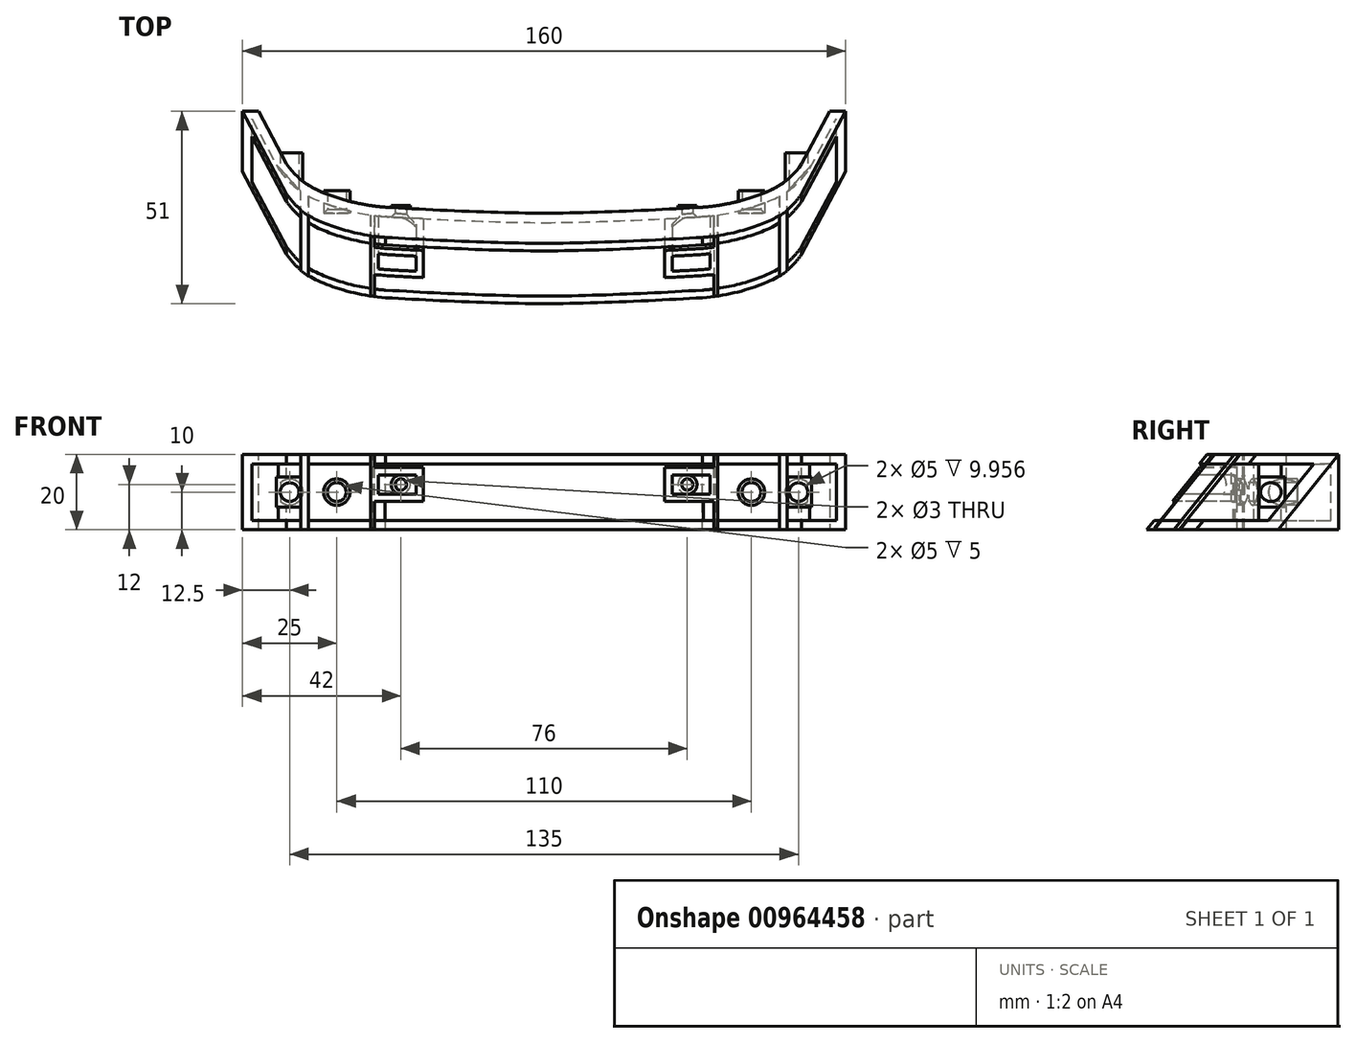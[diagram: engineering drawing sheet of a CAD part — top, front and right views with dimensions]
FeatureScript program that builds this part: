
annotation { "Feature Type Name" : "Feature", "Feature Type Description" : "" }
export const myFeature = defineFeature(function(context is Context, id is Id, definition is map)
    precondition{}
    {
        {
            var Q0;
            Q0=qCreatedBy(makeId("Top.planeOp"),FACE);
            var sketch = newSketch(context, id + "F0", { "sketchPlane" : qUnion([Q0])});
            skLineSegment(sketch, "E0", {"start": v(0, 34.5) * mm, "end": v(0, -43.78) * mm, "construction": true});
            skLineSegment(sketch, "E1", {"start": v(0, 0) * mm, "end": v(-102.6, 0) * mm, "construction": true});
            skLineSegment(sketch, "E2", {"start": v(-80, 0) * mm, "end": v(-80, 40.64) * mm, "construction": true});
            skLineSegment(sketch, "E3", {"start": v(-89.47, 35) * mm, "end": v(0, 35) * mm, "construction": true});
            skLineSegment(sketch, "E4", {"start": v(-80, 35) * mm, "end": v(-68.35, 13.09) * mm});
            skFitSpline(sketch, "E5", {"points": [v(-68.35, 13.09) * mm, v(-59.92, 6.04) * mm, v(-42.03, 1.57) * mm], "startDerivative": vector(19.42, -26.15) * mm, "endDerivative": vector(36.56, -2.64) * mm});
            skFitSpline(sketch, "E6", {"points": [v(-42.03, 1.57) * mm, v(0, 0) * mm], "startDerivative": vector(37.93, -2.25) * mm, "endDerivative": vector(36.74, 0) * mm});
            skPoint(sketch, "E7.orphan", {"position": v(-39.84, -10.44) * mm});
            skPoint(sketch, "E8.orphan", {"position": v(39.84, -10.44) * mm});
            skFitSpline(sketch, "E9.MirrorCS", {"points": [v(42.03, 1.57) * mm, v(0, 0) * mm], "startDerivative": vector(-37.93, -2.25) * mm, "endDerivative": vector(-36.74, 0) * mm});
            skFitSpline(sketch, "E10.MirrorCS", {"points": [v(68.35, 13.09) * mm, v(59.92, 6.04) * mm, v(42.03, 1.57) * mm], "startDerivative": vector(-19.42, -26.15) * mm, "endDerivative": vector(-36.56, -2.64) * mm});
            skLineSegment(sketch, "E11.MirrorCS", {"start": v(80, 35) * mm, "end": v(68.35, 13.09) * mm});
            skSolve(sketch);
        }
        {
            var Q0;
            Q0=qCreatedBy(makeId("Right.planeOp"),FACE);
            var sketch = newSketch(context, id + "F1", { "sketchPlane" : qUnion([Q0])});
            skLineSegment(sketch, "E12", {"start": v(50.4, 0) * mm, "end": v(8, 0) * mm, "construction": true});
            skLineSegment(sketch, "E13", {"start": v(-14.02, 5) * mm, "end": v(0, 5) * mm, "construction": true});
            skLineSegment(sketch, "E14", {"start": v(-14.02, -5) * mm, "end": v(0, -5) * mm, "construction": true});
            skLineSegment(sketch, "E15", {"start": v(0, 18.67) * mm, "end": v(0, 10) * mm, "construction": true});
            skLineSegment(sketch, "E16", {"start": v(8, 18.67) * mm, "end": v(8, -19.69) * mm, "construction": true});
            skLineSegment(sketch, "E17", {"start": v(50.4, -10) * mm, "end": v(-14.02, -10) * mm, "construction": true});
            skLineSegment(sketch, "E18", {"start": v(-14.02, 10) * mm, "end": v(0, 10) * mm, "construction": true});
            skLineSegment(sketch, "E19", {"start": v(0, -10) * mm, "end": v(16, 10) * mm});
            skLineSegment(sketch, "E20", {"start": v(0, -10) * mm, "end": v(24, -10) * mm});
            skLineSegment(sketch, "E21", {"start": v(24, -10) * mm, "end": v(24, 10) * mm});
            skLineSegment(sketch, "E22", {"start": v(24, 10) * mm, "end": v(16, 10) * mm});
            skLineSegment(sketch, "E23.trimOffspring", {"start": v(0, -10) * mm, "end": v(0, -19.69) * mm, "construction": true});
            skLineSegment(sketch, "E24.trimOffspring", {"start": v(4, -5) * mm, "end": v(50.4, -5) * mm, "construction": true});
            skLineSegment(sketch, "E25.trimOffspring", {"start": v(0, 0) * mm, "end": v(-14.02, 0) * mm, "construction": true});
            skLineSegment(sketch, "E26.trimOffspring", {"start": v(12, 5) * mm, "end": v(50.4, 5) * mm, "construction": true});
            skLineSegment(sketch, "E27.trimOffspring", {"start": v(16, 10) * mm, "end": v(50.4, 10) * mm, "construction": true});
            skLineSegment(sketch, "E28", {"start": v(0, -10) * mm, "end": v(0, 10) * mm});
            skLineSegment(sketch, "E29", {"start": v(16, 10) * mm, "end": v(0, 10) * mm});
            skLineSegment(sketch, "E30.bottom", {"start": v(0, 10) * mm, "end": v(-14.02, 10) * mm});
            skLineSegment(sketch, "E30.top", {"start": v(0, -10) * mm, "end": v(-14.02, -10) * mm});
            skLineSegment(sketch, "E30.left", {"start": v(0, 10) * mm, "end": v(0, -10) * mm});
            skLineSegment(sketch, "E30.right", {"start": v(-14.02, 10) * mm, "end": v(-14.02, -10) * mm});
            skSolve(sketch);
        }
        {
            var Q0;
            Q0=makeQuery(id+"F1.imprint","IMPRINT",FACE,{"disambiguationData":[TD([[makeQuery(id+"F1.imprint","IMPRINT",EDGE,{"derivedFrom":sQuery(id+"F1.wireOp",EDGE,"E19")}),-1.0]])]});
            var Q1;
            Q1=sQuery(id+"F0.wireOp",EDGE,"E4");
            var Q2;
            Q2=sQuery(id+"F0.wireOp",EDGE,"E5");
            var Q3;
            Q3=sQuery(id+"F0.wireOp",EDGE,"E6");
            var Q4;
            Q4=sQuery(id+"F0.wireOp",EDGE,"E9.MirrorCS");
            var Q5;
            Q5=sQuery(id+"F0.wireOp",EDGE,"E10.MirrorCS");
            var Q6;
            Q6=sQuery(id+"F0.wireOp",EDGE,"E11.MirrorCS");
            sweep(context, id + "F2", {"profiles" : qUnion([Q0]), "path" : qUnion([Q1, Q2, Q3, Q4, Q5, Q6]), "keepProfileOrientation" : true});
        }
        {
            var Q0;
            Q0=makeQuery(id+"F2.opSweep","SWEPT_FACE",FACE,{"disambiguationData":[OSD([sQuery(id+"F0.wireOp",EDGE,"E4"),sQuery(id+"F1.wireOp",EDGE,"E19")])]});
            var Q1;
            Q1=makeQuery(id+"F2.opSweep","SWEPT_FACE",FACE,{"disambiguationData":[OSD([sQuery(id+"F0.wireOp",EDGE,"E10.MirrorCS"),sQuery(id+"F1.wireOp",EDGE,"E19")])]});
            var Q2;
            Q2=makeQuery(id+"F2.opSweep","SWEPT_FACE",FACE,{"disambiguationData":[OSD([sQuery(id+"F0.wireOp",EDGE,"E11.MirrorCS"),sQuery(id+"F1.wireOp",EDGE,"E19")])]});
            var Q3;
            Q3=makeQuery(id+"F2.opSweep","SWEPT_FACE",FACE,{"disambiguationData":[OSD([sQuery(id+"F0.wireOp",EDGE,"E5"),sQuery(id+"F1.wireOp",EDGE,"E19")])]});
            var Q4;
            Q4=makeQuery(id+"F2.opSweep","SWEPT_FACE",FACE,{"disambiguationData":[OSD([sQuery(id+"F0.wireOp",EDGE,"E6"),sQuery(id+"F1.wireOp",EDGE,"E19")])]});
            var Q5;
            Q5=makeQuery(id+"F2.opSweep","SWEPT_FACE",FACE,{"disambiguationData":[OSD([sQuery(id+"F0.wireOp",EDGE,"E9.MirrorCS"),sQuery(id+"F1.wireOp",EDGE,"E19")])]});
            shell(context, id + "F3", {"entities" : qUnion([Q0, Q1, Q2, Q3, Q4, Q5]), "thickness" : 2.5 * mm});
        }
        {
            var Q0;
            Q0=qCreatedBy(makeId("Right.planeOp"),FACE);
            var sketch = newSketch(context, id + "F4", { "sketchPlane" : qUnion([Q0])});
            skLineSegment(sketch, "E31", {"start": v(0, 25.86) * mm, "end": v(0, -24.93) * mm, "construction": true});
            skLineSegment(sketch, "E32", {"start": v(51, 25.86) * mm, "end": v(51, -24.93) * mm, "construction": true});
            skLineSegment(sketch, "E33", {"start": v(59.89, 25.86) * mm, "end": v(59.89, -24.93) * mm, "construction": true});
            skLineSegment(sketch, "E34", {"start": v(59.89, -13.24) * mm, "end": v(59.89, 11.85) * mm, "construction": true});
            skLineSegment(sketch, "E35", {"start": v(51, 11.85) * mm, "end": v(51, -13.24) * mm, "construction": true});
            skLineSegment(sketch, "E36", {"start": v(59.89, 11.85) * mm, "end": v(59.89, -13.24) * mm});
            skLineSegment(sketch, "E37", {"start": v(51, -13.24) * mm, "end": v(51, 11.85) * mm});
            skLineSegment(sketch, "E38", {"start": v(59.89, 11.85) * mm, "end": v(51, 11.85) * mm});
            skLineSegment(sketch, "E39", {"start": v(51, -13.24) * mm, "end": v(59.89, -13.24) * mm});
            skSolve(sketch);
        }
        {
            var Q0;
            Q0=makeQuery(id+"F4.imprint","IMPRINT",FACE,{"disambiguationData":[TD([[makeQuery(id+"F4.imprint","IMPRINT",EDGE,{"derivedFrom":sQuery(id+"F4.wireOp",EDGE,"E36")}),-1.0]])]});
            extrude(context, id + "F5", {"entities" : qUnion([Q0]), "operationType" : NewBodyOperationType.REMOVE, "endBound" : BoundingType.SYMMETRIC, "oppositeDirection" : true, "depth" : 180 * mm, "offsetDistance" : 25 * mm});
        }
        {
            var Q0;
            Q0=qCreatedBy(makeId("Top.planeOp"),FACE);
            var sketch = newSketch(context, id + "F6", { "sketchPlane" : qUnion([Q0])});
            skLineSegment(sketch, "E40", {"start": v(0, 68.3) * mm, "end": v(0, -66) * mm, "construction": true});
            skLineSegment(sketch, "E41", {"start": v(-80, 68.3) * mm, "end": v(-80, -66) * mm, "construction": true});
            skLineSegment(sketch, "E42", {"start": v(80, 68.3) * mm, "end": v(80, -66) * mm, "construction": true});
            skLineSegment(sketch, "E43", {"start": v(-45, 25.93) * mm, "end": v(-46, 25.93) * mm});
            skLineSegment(sketch, "E44", {"start": v(-46, 25.93) * mm, "end": v(-46, 2.04) * mm});
            skLineSegment(sketch, "E45", {"start": v(-46, 2.04) * mm, "end": v(-45, 2.04) * mm});
            skLineSegment(sketch, "E46", {"start": v(-45, 2.04) * mm, "end": v(-45, 25.93) * mm});
            skLineSegment(sketch, "E47.MirrorCS", {"start": v(45, 25.93) * mm, "end": v(46, 25.93) * mm});
            skLineSegment(sketch, "E48.MirrorCS", {"start": v(46, 25.93) * mm, "end": v(46, 2.04) * mm, "construction": true});
            skLineSegment(sketch, "E49.MirrorCS", {"start": v(45, 25.93) * mm, "end": v(45, 2.04) * mm, "construction": true});
            skLineSegment(sketch, "E50", {"start": v(-45, 25.93) * mm, "end": v(-45, 2.04) * mm});
            skLineSegment(sketch, "E51.MirrorCS", {"start": v(46, 2.04) * mm, "end": v(45, 2.04) * mm});
            skPoint(sketch, "E52.orphan", {"position": v(-45, 68.3) * mm});
            skPoint(sketch, "E53.orphan", {"position": v(-46, 68.3) * mm});
            skPoint(sketch, "E54.orphan", {"position": v(-46, -66) * mm});
            skPoint(sketch, "E55.orphan", {"position": v(-45, -66) * mm});
            skLineSegment(sketch, "E56.MirrorCS", {"start": v(45, 25.93) * mm, "end": v(45, 2.04) * mm});
            skLineSegment(sketch, "E57.MirrorCS", {"start": v(46, 25.93) * mm, "end": v(46, 2.04) * mm});
            skPoint(sketch, "E58.orphan", {"position": v(46, 68.3) * mm});
            skPoint(sketch, "E59.orphan", {"position": v(45, 68.3) * mm});
            skPoint(sketch, "E60.orphan", {"position": v(45, -66) * mm});
            skPoint(sketch, "E61.orphan", {"position": v(46, -66) * mm});
            skSolve(sketch);
        }
        {
            var Q0;
            Q0 = qSketchRegion(id + "F6", true);
            extrude(context, id + "F7", {"entities" : qUnion([Q0]), "operationType" : NewBodyOperationType.ADD, "endBound" : BoundingType.SYMMETRIC, "depth" : 20 * mm, "offsetDistance" : 25 * mm});
        }
        {
            var Q0;
            Q0=makeQuery(id+"F7.opExtrude","SWEPT_FACE",FACE,{"disambiguationData":[OSD([sQuery(id+"F6.wireOp",EDGE,"E44")])]});
            var sketch = newSketch(context, id + "F8", { "sketchPlane" : qUnion([Q0])});
            skLineSegment(sketch, "E62", {"start": v(-18, 10) * mm, "end": v(-2.04, 10) * mm});
            skLineSegment(sketch, "E63", {"start": v(-2.04, 10) * mm, "end": v(-2.04, -9.96) * mm});
            skLineSegment(sketch, "E64", {"start": v(-2.04, -9.96) * mm, "end": v(-18, 10) * mm});
            skSolve(sketch);
        }
        {
            var Q0;
            Q0=qCreatedBy(makeId("Front.planeOp"),FACE);
            var sketch = newSketch(context, id + "F9", { "sketchPlane" : qUnion([Q0])});
            skLineSegment(sketch, "E65", {"start": v(0, 13.76) * mm, "end": v(0, -16.88) * mm, "construction": true});
            skLineSegment(sketch, "E66", {"start": v(-46, 6.5) * mm, "end": v(-46, -2.5) * mm});
            skLineSegment(sketch, "E67", {"start": v(-46, -2.5) * mm, "end": v(-32, -2.5) * mm});
            skLineSegment(sketch, "E68", {"start": v(-32, -2.5) * mm, "end": v(-32, 6.5) * mm});
            skLineSegment(sketch, "E69", {"start": v(-32, 6.5) * mm, "end": v(-46, 6.5) * mm});
            skLineSegment(sketch, "E70", {"start": v(-44, 4.5) * mm, "end": v(-44, -0.5) * mm});
            skLineSegment(sketch, "E71", {"start": v(-44, -0.5) * mm, "end": v(-34, -0.5) * mm});
            skLineSegment(sketch, "E72", {"start": v(-34, -0.5) * mm, "end": v(-34, 4.5) * mm});
            skLineSegment(sketch, "E73", {"start": v(-34, 4.5) * mm, "end": v(-44, 4.5) * mm});
            skLineSegment(sketch, "E74.MirrorCS", {"start": v(32, 6.5) * mm, "end": v(46, 6.5) * mm});
            skLineSegment(sketch, "E75.MirrorCS", {"start": v(46, 6.5) * mm, "end": v(46, -2.5) * mm});
            skLineSegment(sketch, "E76.MirrorCS", {"start": v(46, -2.5) * mm, "end": v(32, -2.5) * mm});
            skLineSegment(sketch, "E77.MirrorCS", {"start": v(32, -2.5) * mm, "end": v(32, 6.5) * mm});
            skLineSegment(sketch, "E78.MirrorCS", {"start": v(34, -0.5) * mm, "end": v(34, 4.5) * mm});
            skLineSegment(sketch, "E79.MirrorCS", {"start": v(34, 4.5) * mm, "end": v(44, 4.5) * mm});
            skLineSegment(sketch, "E80.MirrorCS", {"start": v(44, 4.5) * mm, "end": v(44, -0.5) * mm});
            skLineSegment(sketch, "E81.MirrorCS", {"start": v(44, -0.5) * mm, "end": v(34, -0.5) * mm});
            skLineSegment(sketch, "E82", {"start": v(-81.56, 0) * mm, "end": v(83.03, 0) * mm, "construction": true});
            skSolve(sketch);
        }
        {
            var Q0;
            Q0 = qSketchRegion(id + "F9", true);
            var Q1;
            Q1=makeQuery(id+"F9.imprint","IMPRINT",FACE,{"disambiguationData":[TD([[makeQuery(id+"F9.imprint","IMPRINT",EDGE,{"derivedFrom":sQuery(id+"F9.wireOp",EDGE,"E66")}),1.0]])]});
            extrude(context, id + "F10", {"entities" : qUnion([Q0, Q1]), "operationType" : NewBodyOperationType.ADD, "oppositeDirection" : true, "depth" : 24.5 * mm, "offsetDistance" : 25 * mm});
        }
        {
            var Q0;
            Q0=qCreatedBy(makeId("Right.planeOp"),FACE);
            var sketch = newSketch(context, id + "F11", { "sketchPlane" : qUnion([Q0])});
            skLineSegment(sketch, "E83.bottom", {"start": v(-5.65, 10.74) * mm, "end": v(2.01, 10.74) * mm});
            skLineSegment(sketch, "E83.top", {"start": v(-5.65, -6.02) * mm, "end": v(2.01, -6.02) * mm});
            skLineSegment(sketch, "E83.left", {"start": v(-5.65, 10.74) * mm, "end": v(-5.65, -6.02) * mm});
            skLineSegment(sketch, "E83.right", {"start": v(2.01, 10.74) * mm, "end": v(2.01, -6.02) * mm});
            skSolve(sketch);
        }
        {
            var Q0;
            Q0 = qSketchRegion(id + "F11", true);
            extrude(context, id + "F12", {"entities" : qUnion([Q0]), "operationType" : NewBodyOperationType.REMOVE, "endBound" : BoundingType.SYMMETRIC, "depth" : 100 * mm, "offsetDistance" : 25 * mm});
        }
        {
            var Q0;
            Q0=qCreatedBy(makeId("Front.planeOp"),FACE);
            var sketch = newSketch(context, id + "F13", { "sketchPlane" : qUnion([Q0])});
            skLineSegment(sketch, "E84", {"start": v(0, 29.7) * mm, "end": v(0, -29.07) * mm, "construction": true});
            skLineSegment(sketch, "E85", {"start": v(62.5, 29.7) * mm, "end": v(62.5, -29.07) * mm, "construction": true});
            skLineSegment(sketch, "E86", {"start": v(-83.37, 0) * mm, "end": v(0, 0) * mm, "construction": true});
            skLineSegment(sketch, "E87", {"start": v(-62.5, 10) * mm, "end": v(-64.5, 10) * mm});
            skLineSegment(sketch, "E88", {"start": v(-64.5, 10) * mm, "end": v(-64.5, -10) * mm});
            skLineSegment(sketch, "E89", {"start": v(-64.5, -10) * mm, "end": v(-62.5, -10) * mm});
            skLineSegment(sketch, "E90", {"start": v(-62.5, -10) * mm, "end": v(-62.5, 10) * mm});
            skLineSegment(sketch, "E91.MirrorCS", {"start": v(62.5, -10) * mm, "end": v(62.5, 10) * mm});
            skLineSegment(sketch, "E92.MirrorCS", {"start": v(62.5, 10) * mm, "end": v(64.5, 10) * mm});
            skLineSegment(sketch, "E93.MirrorCS", {"start": v(64.5, 10) * mm, "end": v(64.5, -10) * mm});
            skLineSegment(sketch, "E94.MirrorCS", {"start": v(64.5, -10) * mm, "end": v(62.5, -10) * mm});
            skSolve(sketch);
        }
        {
            var Q0;
            Q0 = qSketchRegion(id + "F13", true);
            extrude(context, id + "F14", {"entities" : qUnion([Q0]), "operationType" : NewBodyOperationType.ADD, "oppositeDirection" : true, "depth" : 30 * mm, "offsetDistance" : 25 * mm});
        }
        {
            var Q0;
            Q0=qCreatedBy(makeId("Top.planeOp"),FACE);
            var sketch = newSketch(context, id + "F15", { "sketchPlane" : qUnion([Q0])});
            skFitSpline(sketch, "E95", {"points": [v(-29.25, 0.78) * mm, v(-42.32, 1.47) * mm, v(-47.66, 2.15) * mm, v(-54.7, 3.85) * mm, v(-61.26, 6.5) * mm, v(-65.24, 9.27) * mm], "startDerivative": vector(-54.73, 2.37) * mm, "endDerivative": vector(-22.49, 17.56) * mm});
            skFitSpline(sketch, "E96", {"points": [v(-29.25, 0.78) * mm, v(-21.3, 0.42) * mm, v(0, 0) * mm], "startDerivative": vector(18.42, -1.02) * mm, "endDerivative": vector(39.34, 0) * mm});
            skLineSegment(sketch, "E97", {"start": v(0, 31.46) * mm, "end": v(0, -16.2) * mm, "construction": true});
            skFitSpline(sketch, "E98.MirrorCS", {"points": [v(29.25, 0.78) * mm, v(21.3, 0.42) * mm, v(0, 0) * mm], "startDerivative": vector(-18.42, -1.02) * mm, "endDerivative": vector(-39.34, 0) * mm});
            skFitSpline(sketch, "E99.MirrorCS", {"points": [v(29.25, 0.78) * mm, v(42.32, 1.47) * mm, v(47.66, 2.15) * mm, v(54.7, 3.85) * mm, v(61.26, 6.5) * mm, v(65.24, 9.27) * mm], "startDerivative": vector(54.73, 2.37) * mm, "endDerivative": vector(22.49, 17.56) * mm});
            skSolve(sketch);
        }
        {
            var Q0;
            Q0=makeQuery(id+"F1.imprint","IMPRINT",FACE,{"disambiguationData":[TD([[makeQuery(id+"F1.imprint","IMPRINT",EDGE,{"derivedFrom":sQuery(id+"F1.wireOp",EDGE,"E19")}),1.0]])]});
            var Q1;
            Q1=makeQuery(id+"F1.imprint","IMPRINT",FACE,{"disambiguationData":[TD([[makeQuery(id+"F1.imprint","IMPRINT",EDGE,{"derivedFrom":sQuery(id+"F1.wireOp",EDGE,"E30.bottom")}),1.0]])]});
            var Q2;
            Q2 = qConstructionFilter(qBodyType(qCreatedBy(id + "F15" ,EDGE), BodyType.WIRE), ConstructionObject.NO);
            sweep(context, id + "F16", {"operationType" : NewBodyOperationType.REMOVE, "profiles" : qUnion([Q0, Q1]), "path" : qUnion([Q2]), "keepProfileOrientation" : true});
        }
        {
            var Q0;
            Q0=qCreatedBy(makeId("Front.planeOp"),FACE);
            var sketch = newSketch(context, id + "F17", { "sketchPlane" : qUnion([Q0])});
            skLineSegment(sketch, "E100", {"start": v(-87.14, 0) * mm, "end": v(85.86, 0) * mm, "construction": true});
            skLineSegment(sketch, "E101", {"start": v(-51.82, 2) * mm, "end": v(50.18, 2) * mm, "construction": true});
            skLineSegment(sketch, "E102", {"start": v(-55, 21.02) * mm, "end": v(-55, -28.71) * mm, "construction": true});
            skLineSegment(sketch, "E103", {"start": v(55, 20.84) * mm, "end": v(55, -28.17) * mm, "construction": true});
            skLineSegment(sketch, "E104", {"start": v(-67.5, 21.56) * mm, "end": v(-67.5, -28.17) * mm, "construction": true});
            skLineSegment(sketch, "E105", {"start": v(67.5, 22.28) * mm, "end": v(67.5, -28.53) * mm, "construction": true});
            skLineSegment(sketch, "E106", {"start": v(-38, 22.1) * mm, "end": v(-38, -28.17) * mm, "construction": true});
            skLineSegment(sketch, "E107", {"start": v(38, 22.1) * mm, "end": v(38, -27.63) * mm, "construction": true});
            skCircle(sketch, "E108", {"center": v(-55, 0) * mm, "radius": 2.5 * mm});
            skCircle(sketch, "E109", {"center": v(-67.5, 0) * mm, "radius": 2.5 * mm});
            skCircle(sketch, "E110", {"center": v(-38, 2) * mm, "radius": 1.5 * mm});
            skCircle(sketch, "E111", {"center": v(38, 2) * mm, "radius": 1.5 * mm});
            skCircle(sketch, "E112", {"center": v(55, 0) * mm, "radius": 2.5 * mm});
            skCircle(sketch, "E113", {"center": v(67.5, 0) * mm, "radius": 2.5 * mm});
            skLineSegment(sketch, "E114", {"start": v(0, 20.99) * mm, "end": v(0, -27.5) * mm, "construction": true});
            skCircle(sketch, "E115", {"center": v(-67.5, 0) * mm, "radius": 3.5 * mm});
            skCircle(sketch, "E116", {"center": v(-55, 0) * mm, "radius": 3.5 * mm});
            skCircle(sketch, "E117", {"center": v(-38, 2) * mm, "radius": 2.5 * mm});
            skCircle(sketch, "E118.MirrorC", {"center": v(38, 2) * mm, "radius": 2.5 * mm});
            skCircle(sketch, "E119.MirrorC", {"center": v(55, 0) * mm, "radius": 3.5 * mm});
            skCircle(sketch, "E120.MirrorC", {"center": v(67.5, 0) * mm, "radius": 3.5 * mm});
            skSolve(sketch);
        }
        {
            var Q0;
            Q0=makeQuery(id+"F17.imprint","IMPRINT",FACE,{"disambiguationData":[TD([[makeQuery(id+"F17.imprint","IMPRINT",EDGE,{"derivedFrom":sQuery(id+"F17.wireOp",EDGE,"E108")}),1.0]])]});
            var Q1;
            Q1=makeQuery(id+"F17.imprint","IMPRINT",FACE,{"disambiguationData":[TD([[makeQuery(id+"F17.imprint","IMPRINT",EDGE,{"derivedFrom":sQuery(id+"F17.wireOp",EDGE,"E109")}),1.0]])]});
            var Q2;
            Q2=makeQuery(id+"F17.imprint","IMPRINT",FACE,{"disambiguationData":[TD([[makeQuery(id+"F17.imprint","IMPRINT",EDGE,{"derivedFrom":sQuery(id+"F17.wireOp",EDGE,"E110")}),1.0]])]});
            var Q3;
            Q3=makeQuery(id+"F17.imprint","IMPRINT",FACE,{"disambiguationData":[TD([[makeQuery(id+"F17.imprint","IMPRINT",EDGE,{"derivedFrom":sQuery(id+"F17.wireOp",EDGE,"E111")}),1.0]])]});
            var Q4;
            Q4=makeQuery(id+"F17.imprint","IMPRINT",FACE,{"disambiguationData":[TD([[makeQuery(id+"F17.imprint","IMPRINT",EDGE,{"derivedFrom":sQuery(id+"F17.wireOp",EDGE,"E112")}),1.0]])]});
            var Q5;
            Q5=makeQuery(id+"F17.imprint","IMPRINT",FACE,{"disambiguationData":[TD([[makeQuery(id+"F17.imprint","IMPRINT",EDGE,{"derivedFrom":sQuery(id+"F17.wireOp",EDGE,"E113")}),1.0]])]});
            extrude(context, id + "F18", {"entities" : qUnion([Q0, Q1, Q2, Q3, Q4, Q5]), "operationType" : NewBodyOperationType.REMOVE, "oppositeDirection" : true, "depth" : 45 * mm, "offsetDistance" : 25 * mm});
        }
        {
            var Q0;
            Q0=qCreatedBy(makeId("Front.planeOp"),FACE);
            var sketch = newSketch(context, id + "F19", { "sketchPlane" : qUnion([Q0])});
            skLineSegment(sketch, "E121", {"start": v(-85.37, 0) * mm, "end": v(87.63, 0) * mm, "construction": true});
            skLineSegment(sketch, "E122", {"start": v(-50.04, 2) * mm, "end": v(51.95, 2) * mm, "construction": true});
            skLineSegment(sketch, "E123", {"start": v(-55, 21.02) * mm, "end": v(-55, -28.71) * mm, "construction": true});
            skLineSegment(sketch, "E124", {"start": v(55, 20.84) * mm, "end": v(55, -28.17) * mm, "construction": true});
            skLineSegment(sketch, "E125", {"start": v(-67.5, 21.56) * mm, "end": v(-67.5, -28.17) * mm, "construction": true});
            skLineSegment(sketch, "E126", {"start": v(67.5, 22.28) * mm, "end": v(67.5, -28.53) * mm, "construction": true});
            skLineSegment(sketch, "E127", {"start": v(-38, 22.1) * mm, "end": v(-38, -28.17) * mm, "construction": true});
            skLineSegment(sketch, "E128", {"start": v(38, 22.1) * mm, "end": v(38, -27.63) * mm, "construction": true});
            skCircle(sketch, "E129", {"center": v(-38, 2) * mm, "radius": 1.5 * mm});
            skCircle(sketch, "E130", {"center": v(38, 2) * mm, "radius": 1.5 * mm});
            skLineSegment(sketch, "E131", {"start": v(0, 20.99) * mm, "end": v(0, -27.5) * mm, "construction": true});
            skCircle(sketch, "E132", {"center": v(-38, 2) * mm, "radius": 2.5 * mm});
            skCircle(sketch, "E133.MirrorC", {"center": v(38, 2) * mm, "radius": 2.5 * mm});
            skSolve(sketch);
        }
        {
            var Q0;
            Q0=qCreatedBy(makeId("Front.planeOp"),FACE);
            var sketch = newSketch(context, id + "F20", { "sketchPlane" : qUnion([Q0])});
            skLineSegment(sketch, "E134", {"start": v(-87.14, 0) * mm, "end": v(85.86, 0) * mm, "construction": true});
            skLineSegment(sketch, "E135", {"start": v(-51.82, 2) * mm, "end": v(50.18, 2) * mm, "construction": true});
            skLineSegment(sketch, "E136", {"start": v(-55, -4.97) * mm, "end": v(-55, -54.71) * mm, "construction": true});
            skLineSegment(sketch, "E137", {"start": v(55, -5.15) * mm, "end": v(55, -54.17) * mm, "construction": true});
            skLineSegment(sketch, "E138", {"start": v(-67.5, -4.43) * mm, "end": v(-67.5, -54.17) * mm, "construction": true});
            skLineSegment(sketch, "E139", {"start": v(67.5, -3.71) * mm, "end": v(67.5, -54.53) * mm, "construction": true});
            skLineSegment(sketch, "E140", {"start": v(-38, -3.9) * mm, "end": v(-38, -54.17) * mm, "construction": true});
            skLineSegment(sketch, "E141", {"start": v(38, -3.9) * mm, "end": v(38, -53.63) * mm, "construction": true});
            skCircle(sketch, "E142", {"center": v(-55, 0) * mm, "radius": 2.5 * mm});
            skCircle(sketch, "E143", {"center": v(55, 0) * mm, "radius": 2.5 * mm});
            skLineSegment(sketch, "E144", {"start": v(0, -5) * mm, "end": v(0, -53.5) * mm, "construction": true});
            skCircle(sketch, "E145", {"center": v(-55, 0) * mm, "radius": 3.5 * mm});
            skCircle(sketch, "E146.MirrorC", {"center": v(55, 0) * mm, "radius": 3.5 * mm});
            skSolve(sketch);
        }
        {
            var Q0;
            Q0=qCreatedBy(makeId("Front.planeOp"),FACE);
            var sketch = newSketch(context, id + "F21", { "sketchPlane" : qUnion([Q0])});
            skLineSegment(sketch, "E147", {"start": v(-87.14, 0) * mm, "end": v(85.86, 0) * mm, "construction": true});
            skLineSegment(sketch, "E148", {"start": v(-51.82, 2) * mm, "end": v(50.18, 2) * mm, "construction": true});
            skLineSegment(sketch, "E149", {"start": v(-55, -0.25) * mm, "end": v(-55, -50) * mm, "construction": true});
            skLineSegment(sketch, "E150", {"start": v(55, -0.43) * mm, "end": v(55, -49.45) * mm, "construction": true});
            skLineSegment(sketch, "E151", {"start": v(-67.5, 0.29) * mm, "end": v(-67.5, -49.45) * mm, "construction": true});
            skLineSegment(sketch, "E152", {"start": v(67.5, 1) * mm, "end": v(67.5, -49.81) * mm, "construction": true});
            skLineSegment(sketch, "E153", {"start": v(-38, 0.83) * mm, "end": v(-38, -49.45) * mm, "construction": true});
            skLineSegment(sketch, "E154", {"start": v(38, 0.83) * mm, "end": v(38, -48.91) * mm, "construction": true});
            skCircle(sketch, "E155", {"center": v(-67.5, 0) * mm, "radius": 2.5 * mm});
            skCircle(sketch, "E156", {"center": v(67.5, 0) * mm, "radius": 2.5 * mm});
            skLineSegment(sketch, "E157", {"start": v(0, -0.3) * mm, "end": v(0, -48.78) * mm, "construction": true});
            skCircle(sketch, "E158", {"center": v(-67.5, 0) * mm, "radius": 3.5 * mm});
            skCircle(sketch, "E159.MirrorC", {"center": v(67.5, 0) * mm, "radius": 3.5 * mm});
            skSolve(sketch);
        }
        {
            var Q0;
            Q0 = qSketchRegion(id + "F19", true);
            extrude(context, id + "F22", {"entities" : qUnion([Q0]), "operationType" : NewBodyOperationType.ADD, "oppositeDirection" : true, "depth" : 26 * mm, "offsetDistance" : 25 * mm, "hasSecondDirection" : true, "secondDirectionOppositeDirection" : true, "secondDirectionDepth" : 25 * mm});
        }
        {
            var Q0;
            {var subQ0=sQuery(id+"F1.wireOp",EDGE,"E21");Q0=makeQuery(id+"F18.boolean.opBoolean","INTERSECT",EDGE,{"derivedFrom":[makeQuery(id+"F10.boolean.opBoolean","SPLIT",FACE,{"disambiguationData":[TD([makeQuery(id+"F10.opExtrude","SWEPT_FACE",FACE,{"disambiguationData":[OSD([sQuery(id+"F9.wireOp",EDGE,"E71")])]})])],"derivedFrom":makeQuery(id+"F3.opShell","OFFSET_FACE",FACE,{"disambiguationData":[OSD([sQuery(id+"F0.wireOp",EDGE,"E6"),subQ0])]})}),makeQuery(id+"F18.opExtrude","SWEPT_FACE",FACE,{"disambiguationData":[OSD([sQuery(id+"F17.wireOp",EDGE,"E110")])]})]});}
            var Q1;
            {var subQ0=sQuery(id+"F1.wireOp",EDGE,"E21");Q1=makeQuery(id+"F18.boolean.opBoolean","INTERSECT",EDGE,{"derivedFrom":[makeQuery(id+"F10.boolean.opBoolean","SPLIT",FACE,{"disambiguationData":[TD([makeQuery(id+"F10.opExtrude","SWEPT_FACE",FACE,{"disambiguationData":[OSD([sQuery(id+"F9.wireOp",EDGE,"E78.MirrorCS")])]})])],"derivedFrom":makeQuery(id+"F3.opShell","OFFSET_FACE",FACE,{"disambiguationData":[OSD([sQuery(id+"F0.wireOp",EDGE,"E9.MirrorCS"),subQ0])]})}),makeQuery(id+"F18.opExtrude","SWEPT_FACE",FACE,{"disambiguationData":[OSD([sQuery(id+"F17.wireOp",EDGE,"E111")])]})]});}
            chamfer(context, id + "F23", {"entities" : qUnion([Q0, Q1]), "width" : 1 * mm, "tangentPropagation" : true});
        }
        {
            var Q0;
            Q0 = qSketchRegion(id + "F20", true);
            extrude(context, id + "F24", {"entities" : qUnion([Q0]), "operationType" : NewBodyOperationType.ADD, "oppositeDirection" : true, "depth" : 30 * mm, "offsetDistance" : 25 * mm, "hasSecondDirection" : true, "secondDirectionOppositeDirection" : true, "secondDirectionDepth" : 24 * mm});
        }
        {
            var Q0;
            Q0=makeQuery(id+"F24.opExtrude","CAP_EDGE",EDGE,{"disambiguationData":[OSD([sQuery(id+"F20.wireOp",EDGE,"E142")])],"isStart":true});
            var Q1;
            Q1=makeQuery(id+"F24.opExtrude","CAP_EDGE",EDGE,{"disambiguationData":[OSD([sQuery(id+"F20.wireOp",EDGE,"E143")])],"isStart":true});
            chamfer(context, id + "F25", {"entities" : qUnion([Q0, Q1]), "width" : 1 * mm, "tangentPropagation" : true});
        }
        {
            var Q0;
            Q0 = qSketchRegion(id + "F21", true);
            extrude(context, id + "F26", {"entities" : qUnion([Q0]), "operationType" : NewBodyOperationType.ADD, "oppositeDirection" : true, "depth" : 40 * mm, "offsetDistance" : 25 * mm, "hasSecondDirection" : true, "secondDirectionOppositeDirection" : true, "secondDirectionDepth" : 30 * mm});
        }
        {
            var Q0;
            Q0=qCreatedBy(makeId("Top.planeOp"),FACE);
            var sketch = newSketch(context, id + "F27", { "sketchPlane" : qUnion([Q0])});
            skLineSegment(sketch, "E160", {"start": v(-71.02, 36.86) * mm, "end": v(-71.02, 26.53) * mm});
            skLineSegment(sketch, "E161", {"start": v(-71.02, 26.53) * mm, "end": v(-64.59, 26.53) * mm});
            skLineSegment(sketch, "E162", {"start": v(-64.59, 26.53) * mm, "end": v(-64.6, 29.8) * mm});
            skLineSegment(sketch, "E163", {"start": v(-71.02, 36.86) * mm, "end": v(-64.6, 29.8) * mm});
            skPoint(sketch, "E164.orphan", {"position": v(-71.02, 39.72) * mm});
            skPoint(sketch, "E165.orphan", {"position": v(-64.6, 30.92) * mm});
            skLineSegment(sketch, "E166.MirrorCS", {"start": v(71.02, 36.86) * mm, "end": v(64.6, 29.8) * mm});
            skLineSegment(sketch, "E167.MirrorCS", {"start": v(64.59, 26.53) * mm, "end": v(64.6, 29.8) * mm});
            skLineSegment(sketch, "E168.MirrorCS", {"start": v(71.02, 26.53) * mm, "end": v(64.59, 26.53) * mm});
            skLineSegment(sketch, "E169.MirrorCS", {"start": v(71.02, 36.86) * mm, "end": v(71.02, 26.53) * mm});
            skSolve(sketch);
        }
        {
            var Q0;
            Q0 = qSketchRegion(id + "F27", true);
            extrude(context, id + "F28", {"entities" : qUnion([Q0]), "operationType" : NewBodyOperationType.REMOVE, "endBound" : BoundingType.SYMMETRIC, "oppositeDirection" : true, "depth" : 8 * mm, "offsetDistance" : 25 * mm});
        }
    });
